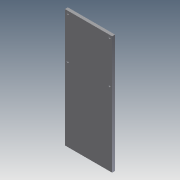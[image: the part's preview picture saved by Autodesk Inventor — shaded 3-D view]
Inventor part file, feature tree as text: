
AUTODESK INVENTOR PART (.ipt)
format: ipt  version: 2011 (Build 150239000, 239)  size: 111,104 bytes
history: native  units: in
note: dims shown in document units (in); Inventor stores cm internally (conversion verified against a paired STEP export)
features: extrude x2, sketch x2
ambient origin geometry x8: Origin, YZ Plane, XZ Plane, XY Plane, X Axis, Y Axis, Z Axis, Center Point
bodies: Solid1 (feature_tree)
feature tree (4):
  extrude  "Extrusion1"  Depth=10.0in
  extrude  "Extrusion2"  Depth=0.235in
  sketch  "Sketch1"  dims[d0=4.0in d1=10.0in]
  sketch  "Sketch2"  dims[d2=0.235in d3=0.235in d4=0.235in d5=3.53in d6=0.156in d7=0.25in d8=0.0in d9=1.0in d10=0.0in]
